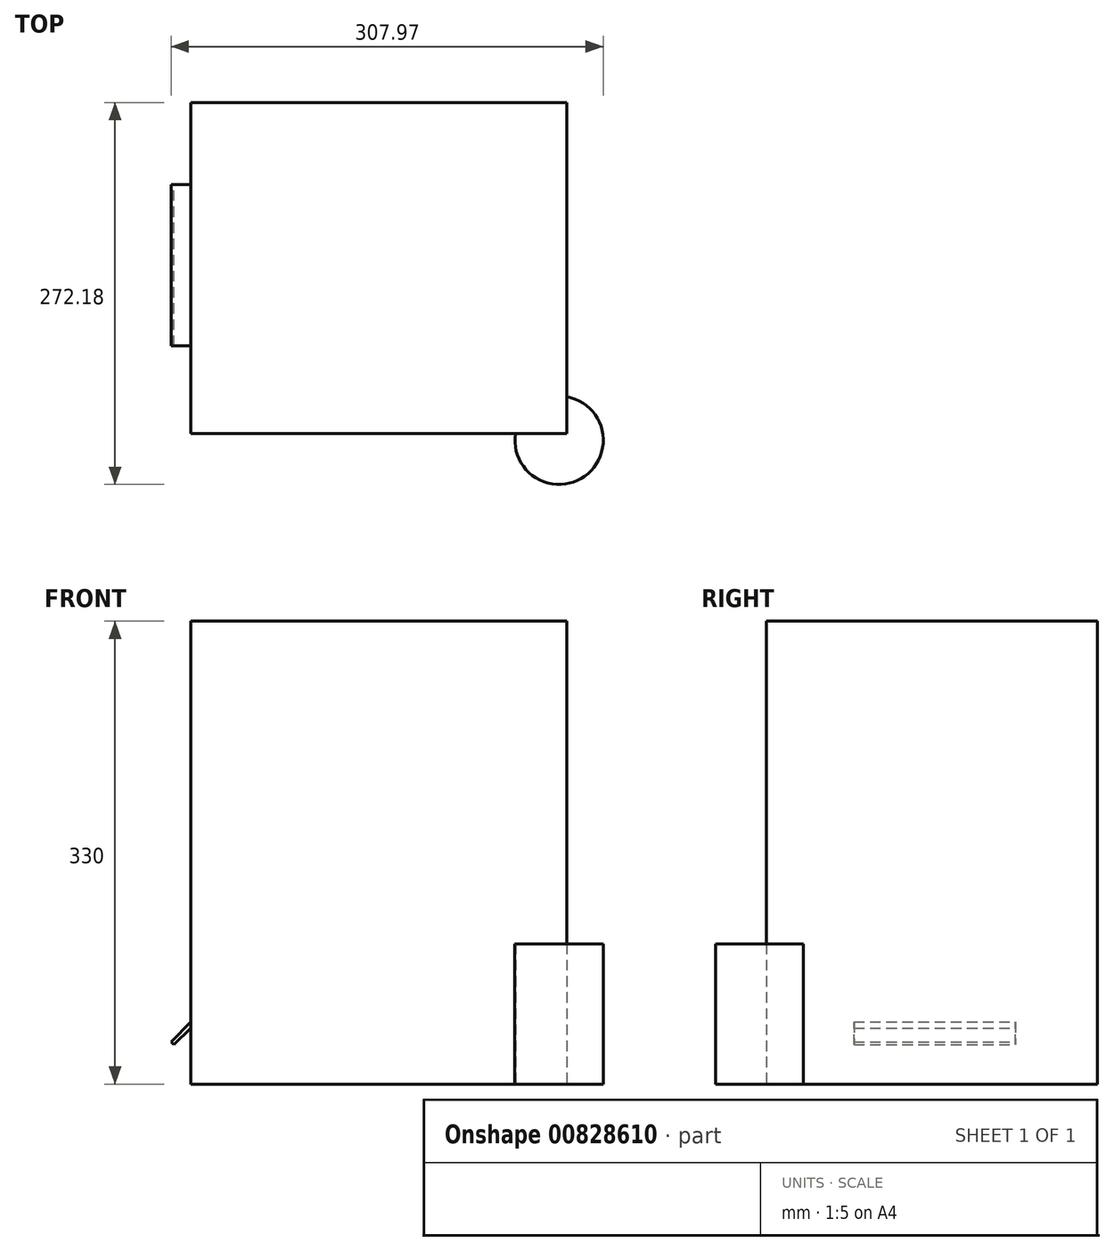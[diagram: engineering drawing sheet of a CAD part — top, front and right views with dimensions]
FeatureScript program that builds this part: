
annotation { "Feature Type Name" : "Feature", "Feature Type Description" : "" }
export const myFeature = defineFeature(function(context is Context, id is Id, definition is map)
    precondition{}
    {
        {
            var Q0;
            Q0=qCreatedBy(makeId("Top.planeOp"),FACE);
            var sketch = newSketch(context, id + "F0", { "sketchPlane" : qUnion([Q0])});
            skLineSegment(sketch, "E0.bottom", {"start": v(-137, -135) * mm, "end": v(131, -135) * mm});
            skLineSegment(sketch, "E0.top", {"start": v(-137, 101) * mm, "end": v(131, 101) * mm});
            skLineSegment(sketch, "E0.left", {"start": v(-137, -135) * mm, "end": v(-137, 101) * mm});
            skLineSegment(sketch, "E0.right", {"start": v(131, -135) * mm, "end": v(131, 101) * mm});
            skPoint(sketch, "E0.middle", {"position": v(-3, -17) * mm});
            skCircle(sketch, "E1", {"center": v(125.4, -139.68) * mm, "radius": 31.5 * mm});
            skSolve(sketch);
        }
        {
            var Q0;
            {var subQ1=sQuery(id+"F0.wireOp",EDGE,"E0.top");Q0=makeQuery(id+"F0.imprint","IMPRINT",FACE,{"disambiguationData":[TD([[makeQuery(id+"F0.imprint","IMPRINT",EDGE,{"derivedFrom":subQ1}),-1.0]])]});}
            var Q1;
            {var subQ0=sQuery(id+"F0.wireOp",EDGE,"E0.right");var subQ1=sQuery(id+"F0.wireOp",EDGE,"E0.bottom");var subQ2=makeQuery(id+"F0.imprint","INTERSECT",VERTEX,{"derivedFrom":[subQ1,subQ0]});Q1=makeQuery(id+"F0.imprint","IMPRINT",FACE,{"disambiguationData":[TD([[makeQuery(id+"F0.imprint","IMPRINT",EDGE,{"disambiguationData":[TD([[subQ2,1.0]])],"derivedFrom":subQ1}),1.0]])]});}
            extrude(context, id + "F1", {"entities" : qUnion([Q0, Q1]), "depth" : 330 * mm, "offsetDistance" : 25 * mm});
        }
        {
            var Q0;
            {var subQ0=sQuery(id+"F0.wireOp",EDGE,"E0.right");var subQ1=sQuery(id+"F0.wireOp",EDGE,"E0.bottom");var subQ2=makeQuery(id+"F0.imprint","INTERSECT",VERTEX,{"derivedFrom":[subQ1,subQ0]});Q0=makeQuery(id+"F0.imprint","IMPRINT",FACE,{"disambiguationData":[TD([[makeQuery(id+"F0.imprint","IMPRINT",EDGE,{"disambiguationData":[TD([[subQ2,1.0]])],"derivedFrom":subQ1}),-1.0]])]});}
            extrude(context, id + "F2", {"entities" : qUnion([Q0]), "operationType" : NewBodyOperationType.ADD, "depth" : 100 * mm, "offsetDistance" : 25 * mm});
        }
        {
            var Q0;
            Q0=qCreatedBy(makeId("Front.planeOp"),FACE);
            var sketch = newSketch(context, id + "F3", { "sketchPlane" : qUnion([Q0])});
            skLineSegment(sketch, "E2", {"start": v(-151.07, 30.12) * mm, "end": v(-148.95, 28) * mm});
            skLineSegment(sketch, "E3", {"start": v(-148.95, 28) * mm, "end": v(-134.88, 42.07) * mm});
            skLineSegment(sketch, "E4", {"start": v(-134.88, 42.07) * mm, "end": v(-137, 44.2) * mm});
            skLineSegment(sketch, "E5", {"start": v(-137, 44.2) * mm, "end": v(-151.07, 30.12) * mm});
            skSolve(sketch);
        }
        {
            var Q0;
            Q0=makeQuery(id+"F3.imprint","IMPRINT",FACE,{"disambiguationData":[TD([[makeQuery(id+"F3.imprint","IMPRINT",EDGE,{"derivedFrom":sQuery(id+"F3.wireOp",EDGE,"E2")}),1.0]])]});
            extrude(context, id + "F4", {"entities" : qUnion([Q0]), "operationType" : NewBodyOperationType.ADD, "depth" : 72.5 * mm, "offsetDistance" : 25 * mm, "hasSecondDirection" : true, "secondDirectionOppositeDirection" : true, "secondDirectionDepth" : 42.5 * mm});
        }
    });
